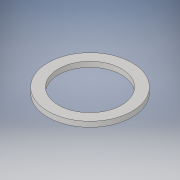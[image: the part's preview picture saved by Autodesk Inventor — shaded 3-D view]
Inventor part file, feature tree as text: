
AUTODESK INVENTOR PART (.ipt)
format: ipt  version: 2018 (Build 220112000, 112)  size: 99,328 bytes
history: native  units: in
note: dims shown in document units (in); Inventor stores cm internally (conversion verified against a paired STEP export)
features: extrude x1, sketch x1
ambient origin geometry x8: Origin, YZ Plane, XZ Plane, XY Plane, X Axis, Y Axis, Z Axis, Center Point
bodies: Solid1 (feature_tree)
feature tree (2):
  extrude  "Extrusion1"  Depth=0.05in
  sketch  "Sketch1"  dims[d0=0.6in d1=0.8in d2=0.05in d3=0.0in]
